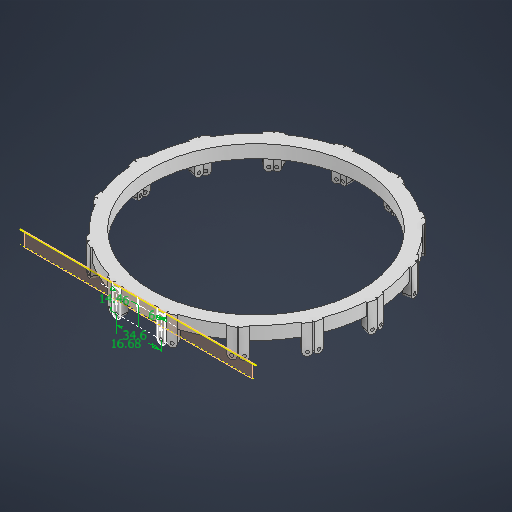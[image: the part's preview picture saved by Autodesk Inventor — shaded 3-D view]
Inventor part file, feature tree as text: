
AUTODESK INVENTOR PART (.ipt)
format: ipt  version: 2025.1 (Build 291241020, 241B)  size: 463,360 bytes
history: native  units: mm
features: extrude x2, sketch x2, plane x1, hole x1, pattern_circular x1, projected_geometry x1
ambient origin geometry x8: Origin, YZ Plane, XZ Plane, XY Plane, X Axis, Y Axis, Z Axis, Center Point
bodies: Solid1 (feature_tree)
feature tree (8):
  extrude  "Extrusion1"  Depth=10.0mm
  plane  "Work Plane1"
  sketch  "Sketch2"  dims[d2=10.0mm d3=0.0mm d4=34.6mm d5=16.68mm d6=14.4mm d7=6.0mm d8=6.0mm d9=6.0mm d10=0.0mm d11=2.459mm d12=6.0mm d13=4.0mm d14=2.0mm d15=90.0deg d16=8.0mm d17=20.594885mm d18=140.0mm d19=360.0deg]
  extrude  "Extrusion2"  Depth=34.6mm
  hole  "Hole1"  [1 undecoded]
  pattern_circular  "Circular Pattern1"  [2 undecoded]
  sketch  "Sketch1"  dims[d0=182.0mm d1=10.0mm]
  projected_geometry  "Projected Loop1"
note: 3 required parameter values undecoded (feature->parameter linkage not recoverable at this tier; creation-order binding heuristic only, values carry confidence <= 0.55)
